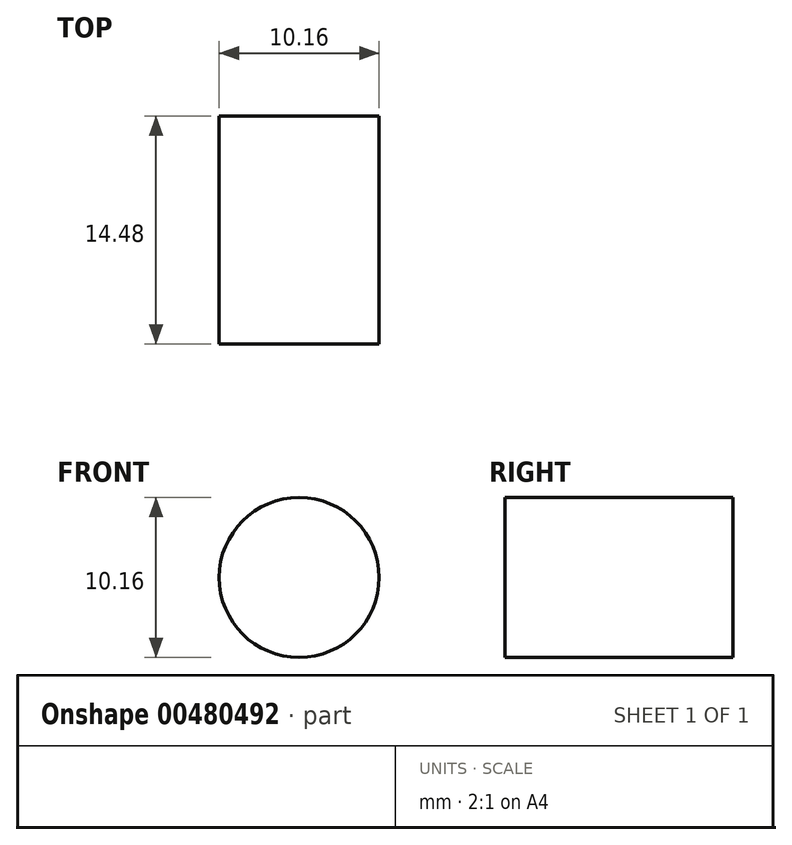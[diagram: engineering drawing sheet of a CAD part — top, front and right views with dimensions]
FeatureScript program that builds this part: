
annotation { "Feature Type Name" : "Feature", "Feature Type Description" : "" }
export const myFeature = defineFeature(function(context is Context, id is Id, definition is map)
    precondition{}
    {
        {
            var Q0;
            Q0=qCreatedBy(makeId("Front.planeOp"),FACE);
            var sketch = newSketch(context, id + "F0", { "sketchPlane" : qUnion([Q0])});
            skCircle(sketch, "E0", {"center": v(0, 0) * mm, "radius": 5.08 * mm});
            skSolve(sketch);
        }
        {
            var Q0;
            Q0 = qSketchRegion(id + "F0", true);
            extrude(context, id + "F1", {"entities" : qUnion([Q0]), "depth" : 14.48 * mm});
        }
    });
